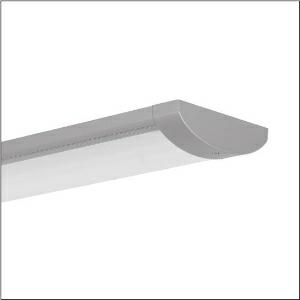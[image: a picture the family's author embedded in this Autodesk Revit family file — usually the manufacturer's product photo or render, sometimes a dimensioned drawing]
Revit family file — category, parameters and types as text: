
# Revit family: tv_20_5xa861d2n0a
name_source: partatom
category: Lighting Fixtures
units: mm (PartAtom-declared; Revit-internal decimal feet)

## family parameters
Cut with Voids When Loaded = No
Host = Face
Light Source = No
Part Type = Normal
Room Calculation Point = No
Round Connector Dimension = Use Diameter
Shared = No

## types (1)
- TV 20 (1 x LED 4000K / CRI = 80 (unbekannt), 2130 lm, 4000K)
    Apparent Load = 21 VA
    CIE Flux Codes = 48 78 95 99 100
    Color Rendering = 80
    Color Temperature = 4000K
    Default Elevation = 1800 mm
    Description = TV 20, vandal-proof luminaire, primary light control with specular reflector, of aluminium, matt, primary optical cover: enclosure, of PC, frosted, light emission: direct distribution, primary light characteristic: symmetric, installation type: surface-mounted, LED rated luminous flux: 2.130 lm, light colour: 840, colour temperature: 4000K, control gear: ECG DALI, mains connection: 230V, AC, 50Hz, rated input power: 21W, luminaire housing, of aluminium, coated, Siteco® metallic grey (DB 702S), length: 705 mm, width: 260 mm, height: 70mm, protection rating (complete): IP65, insulation class (complete): insulation class I (protective earthing), certification: CE, protection symbol: F, impact resistance: 2x IK10, standard: EN 60598, packaging unit: 1 piece
    Height = 70 mm
    Lamp = 1 x LED 4000K / CRI >= 80 (unbekannt)
    Lamp Light Flux = 2130 lm
    Lamp count = 1
    Length = 705 mm
    Luminous efficacy = 101 lm/W
    Manufacturer = Siteco
    ModVariant = No
    Model = 5XA861D2N0A
    Mounting Place = Ceiling
    Mounting Type = Surface mounted
    Number of Poles = 1
    OnlyDefault = Yes
    Power Factor = 1
    Product Name = TV 20
    Product group = vandal-proof luminaire
    ProductGroupID = 307
    Protection Class = Protection class I
    Protection Degree = IP 65
    RLX_Detail_Level = 1
    RlxData = <blob elided: 34137 chars, md5=0f2a3b31>
    Socket = socket
    Standby Power = 0 W
    System Light Flux = 2130 lm
    System Power = 21 W
    Type Comments = Product without accessories
    Type Image = l_1004809.jpg
    URL = http://relux.com
    VarID = ---
    Voltage = 0 V
    Weight = 0.00 kg
    Width = 260 mm

## geometry (parser evidence)
native form markers: Blend x4, Sweep x10
no freeform markers — native parametric forms only
